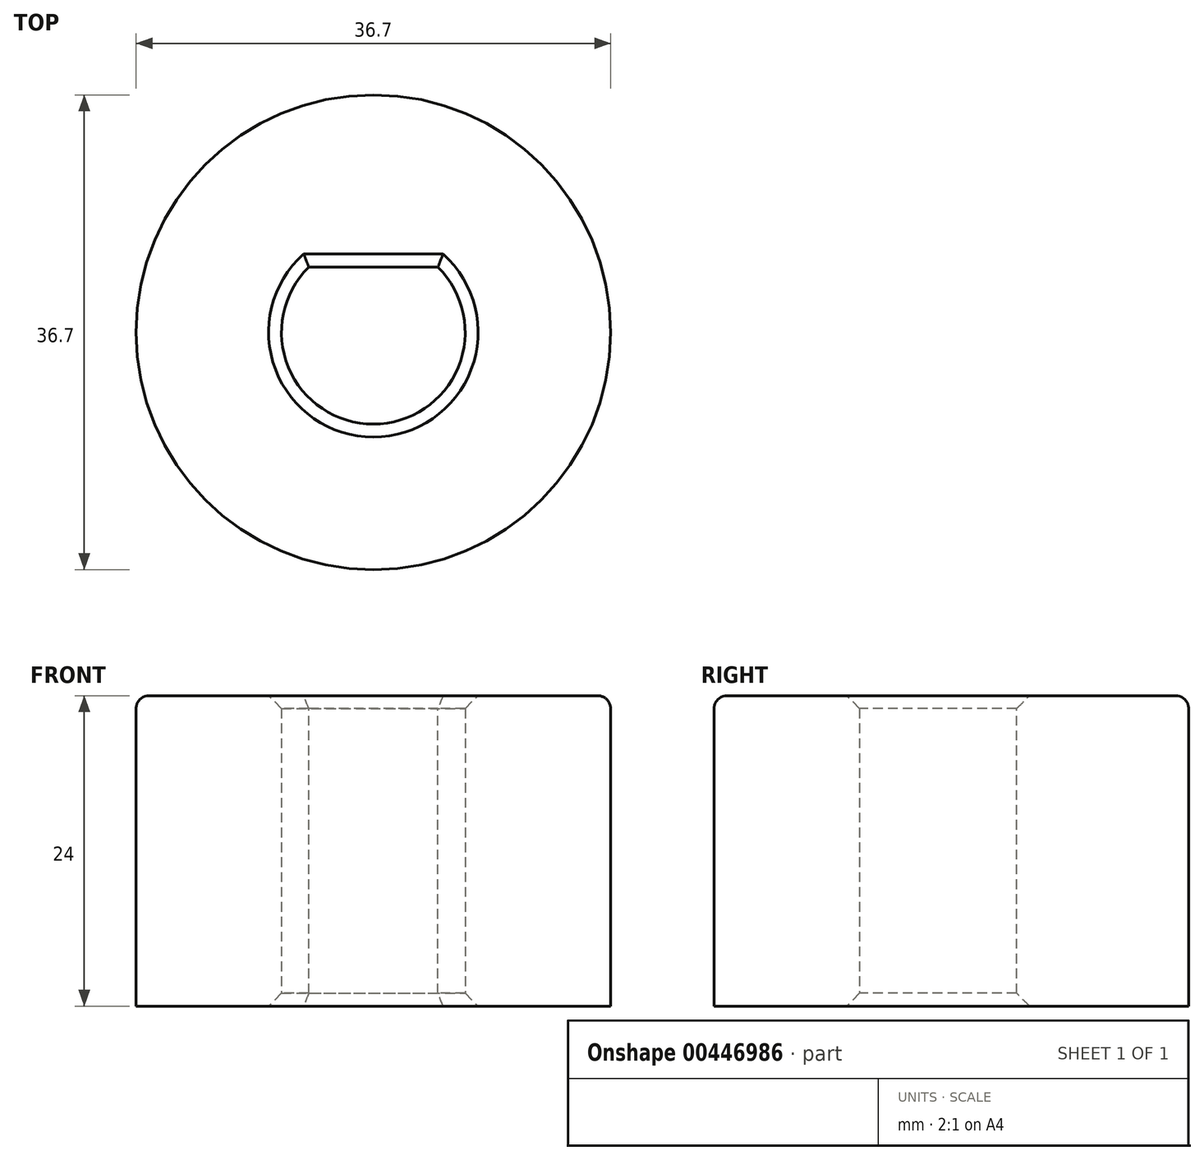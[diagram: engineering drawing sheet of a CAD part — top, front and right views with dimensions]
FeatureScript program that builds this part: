
annotation { "Feature Type Name" : "Feature", "Feature Type Description" : "" }
export const myFeature = defineFeature(function(context is Context, id is Id, definition is map)
    precondition{}
    {
        {
            var Q0;
            Q0=qCreatedBy(makeId("Top.planeOp"),FACE);
            var sketch = newSketch(context, id + "F0", { "sketchPlane" : qUnion([Q0])});
            skCircle(sketch, "E0", {"center": v(0, 0) * mm, "radius": 18.35 * mm});
            skCircle(sketch, "E1", {"center": v(0, 0) * mm, "radius": 7.1 * mm});
            skSolve(sketch);
        }
        {
            var Q0;
            Q0=makeQuery(id+"F0.imprint","IMPRINT",FACE,{"disambiguationData":[TD([[makeQuery(id+"F0.imprint","IMPRINT",EDGE,{"derivedFrom":sQuery(id+"F0.wireOp",EDGE,"E0")}),1.0]])]});
            extrude(context, id + "F1", {"entities" : qUnion([Q0]), "depth" : 24 * mm});
        }
        {
            var Q0;
            Q0=makeQuery(id+"F1.opExtrude","CAP_FACE",FACE,{"disambiguationData":[OSD([sQuery(id+"F0.wireOp",EDGE,"E0"),sQuery(id+"F0.wireOp",EDGE,"E1")])],"isStart":false});
            var sketch = newSketch(context, id + "F2", { "sketchPlane" : qUnion([Q0])});
            skLineSegment(sketch, "E2.top", {"start": v(-5, 5.05) * mm, "end": v(5, 5.05) * mm});
            skPoint(sketch, "E2.middle", {"position": v(0, 0) * mm});
            skSolve(sketch);
        }
        {
            var Q0;
            {var subQ0=sQuery(id+"F2.wireOp",EDGE,"E2.top");Q0=makeQuery(id+"F2.imprint","IMPRINT",FACE,{"disambiguationData":[TD([[makeQuery(id+"F2.imprint","IMPRINT",EDGE,{"derivedFrom":subQ0}),1.0]])]});}
            extrude(context, id + "F3", {"entities" : qUnion([Q0]), "operationType" : NewBodyOperationType.ADD, "oppositeDirection" : true, "depth" : 24 * mm});
        }
        {
            var Q0;
            Q0=makeQuery(id+"F3.opExtrude","CAP_EDGE",EDGE,{"disambiguationData":[OSD([sQuery(id+"F2.wireOp",EDGE,"E2.top")])],"isStart":true});
            var Q1;
            Q1=makeQuery(id+"F1.opExtrude","CAP_EDGE",EDGE,{"disambiguationData":[OSD([sQuery(id+"F0.wireOp",EDGE,"E1")])],"isStart":false});
            chamfer(context, id + "F4", {"entities" : qUnion([Q0, Q1]), "width" : 1 * mm, "tangentPropagation" : true});
        }
        {
            var Q0;
            Q0=makeQuery(id+"F3.opExtrude","CAP_EDGE",EDGE,{"disambiguationData":[OSD([sQuery(id+"F2.wireOp",EDGE,"E2.top")])],"isStart":false});
            var Q1;
            Q1=makeQuery(id+"F1.opExtrude","CAP_EDGE",EDGE,{"disambiguationData":[OSD([sQuery(id+"F0.wireOp",EDGE,"E1")])],"isStart":true});
            chamfer(context, id + "F5", {"entities" : qUnion([Q0, Q1]), "chamferType" : ChamferType.OFFSET_ANGLE, "width" : 1 * mm, "oppositeDirection" : false, "angle" : 45 * degree, "tangentPropagation" : true});
        }
        {
            var Q0;
            Q0=makeQuery(id+"F1.opExtrude","CAP_EDGE",EDGE,{"disambiguationData":[OSD([sQuery(id+"F0.wireOp",EDGE,"E0")])],"isStart":false});
            fillet(context, id + "F6", {"entities" : qUnion([Q0]), "radius" : 1 * mm, "tangentPropagation" : true, "allowEdgeOverflow" : false});
        }
    });
